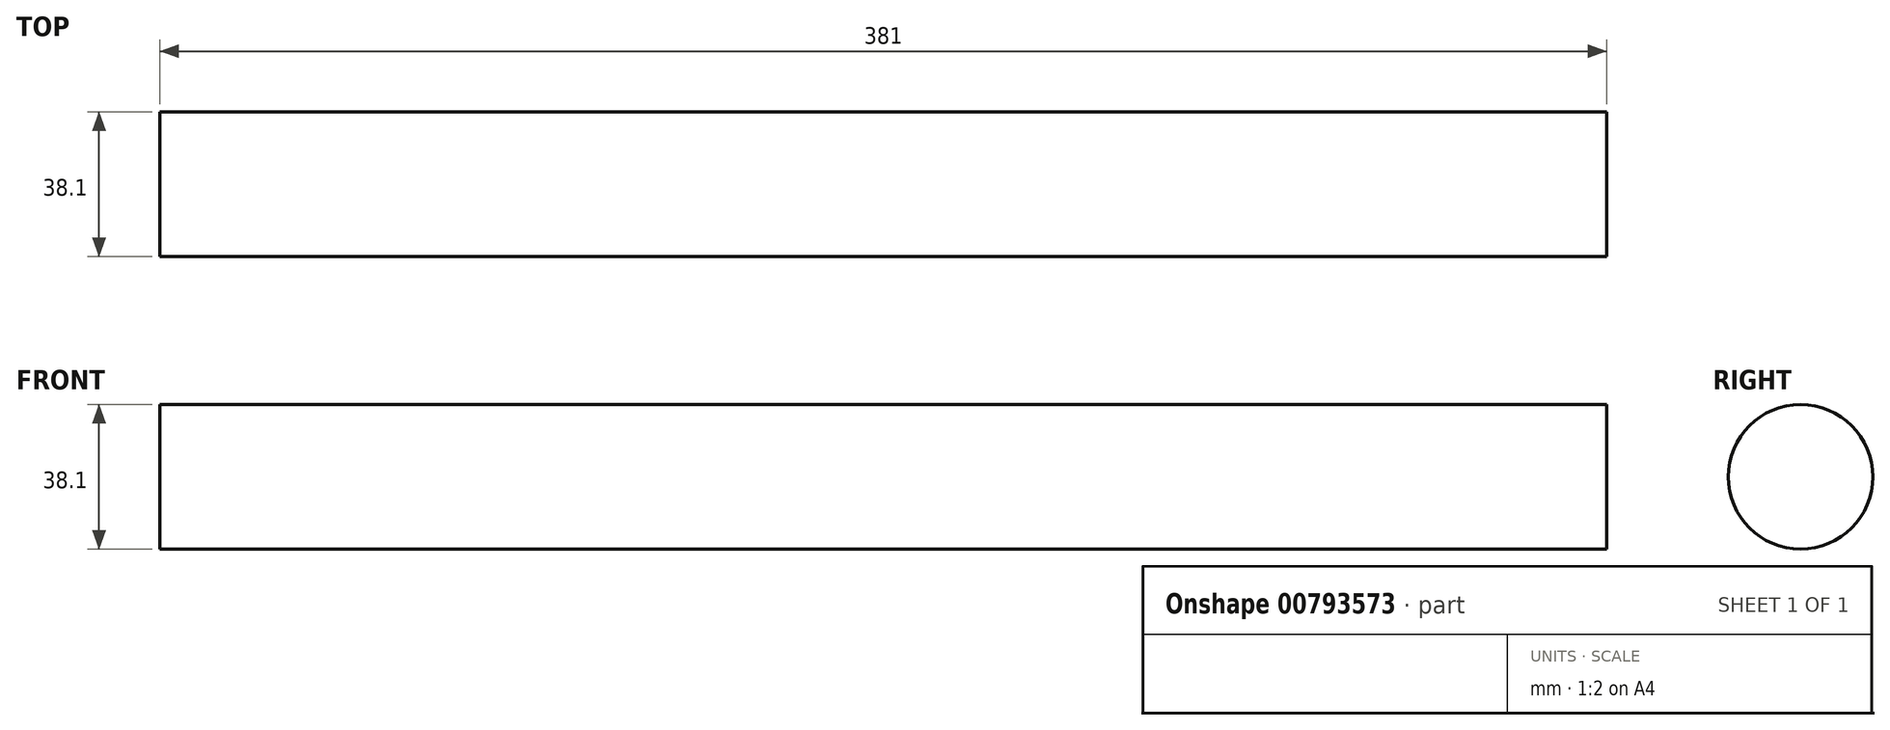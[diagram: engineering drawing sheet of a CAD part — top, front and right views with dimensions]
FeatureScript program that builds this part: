
annotation { "Feature Type Name" : "Feature", "Feature Type Description" : "" }
export const myFeature = defineFeature(function(context is Context, id is Id, definition is map)
    precondition{}
    {
        {
            var Q0;
            Q0=qCreatedBy(makeId("Right.planeOp"),FACE);
            var sketch = newSketch(context, id + "F0", { "sketchPlane" : qUnion([Q0])});
            skCircle(sketch, "E0", {"center": v(0, 0) * mm, "radius": 19.05 * mm});
            skSolve(sketch);
        }
        {
            var Q0;
            Q0 = qSketchRegion(id + "F0", true);
            extrude(context, id + "F1", {"entities" : qUnion([Q0]), "depth" : 190.5 * mm, "offsetDistance" : 25.4 * mm, "hasSecondDirection" : true, "secondDirectionOppositeDirection" : true, "secondDirectionDepth" : 190.5 * mm});
        }
    });
